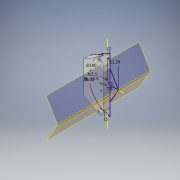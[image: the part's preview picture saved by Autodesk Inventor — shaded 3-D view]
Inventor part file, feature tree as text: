
AUTODESK INVENTOR PART (.ipt)
format: ipt  version: 2019.3 (Build 233278000, 278)  size: 193,024 bytes
history: native  units: mm
features: sketch x7, sweep x3, plane x2, chamfer x2, extrude x1, hole x1
ambient origin geometry x8: Origin, YZ Plane, XZ Plane, XY Plane, X Axis, Y Axis, Z Axis, Center Point
bodies: Solid1 (feature_tree)
feature tree (16):
  extrude  "Extrusion1"  Depth=7.5mm
  sketch  "Sketch3"  dims[d3=51.29mm d11=7.5mm]
  sketch  "Sketch4"  dims[d12=7.5mm d13=12.5mm]
  plane  "Work Plane1"
  plane  "Work Plane2"
  sketch  "Sketch5"  dims[d14=12.5mm d15=30.0mm d16=0.0mm]
  sweep  "Sweep1"
  sweep  "Sweep2"
  sweep  "Sweep3"
  chamfer  "Chamfer1"  Distance=5.0mm
  chamfer  "Chamfer2"  [1 undecoded]
  hole  "Hole1"  [1 undecoded]
  sketch  "Sketch6"  dims[d21=60.0deg d22=60.0deg]
  sketch  "Sketch7"  dims[d23=5.1mm]
  sketch  "Sketch8"  dims[d24=10.2mm]
  sketch  "Sketch10"  dims[d25=14.424978mm d26=5.0mm d29=0.0mm d30=0.0mm d31=5.1mm d32=14.424978mm d33=10.2mm d34=5.0mm d35=0.0mm d36=0.0mm d37=5.1mm d38=10.2mm d39=14.424978mm d40=5.0mm d41=0.0mm d42=0.0mm d44=12.0mm d45=15.0mm d46=40.0mm d47=2.0mm d48=30.0deg d49=40.0mm d50=2.0mm d51=30.0deg d53=10.0mm d54=10.0mm d55=10.0mm d56=7.5mm d57=6.0mm d58=13.5mm d59=5.0mm d60=90.0deg d61=8.0mm d62=20.594885mm]
note: 2 required parameter values undecoded (feature->parameter linkage not recoverable at this tier; creation-order binding heuristic only, values carry confidence <= 0.55)
